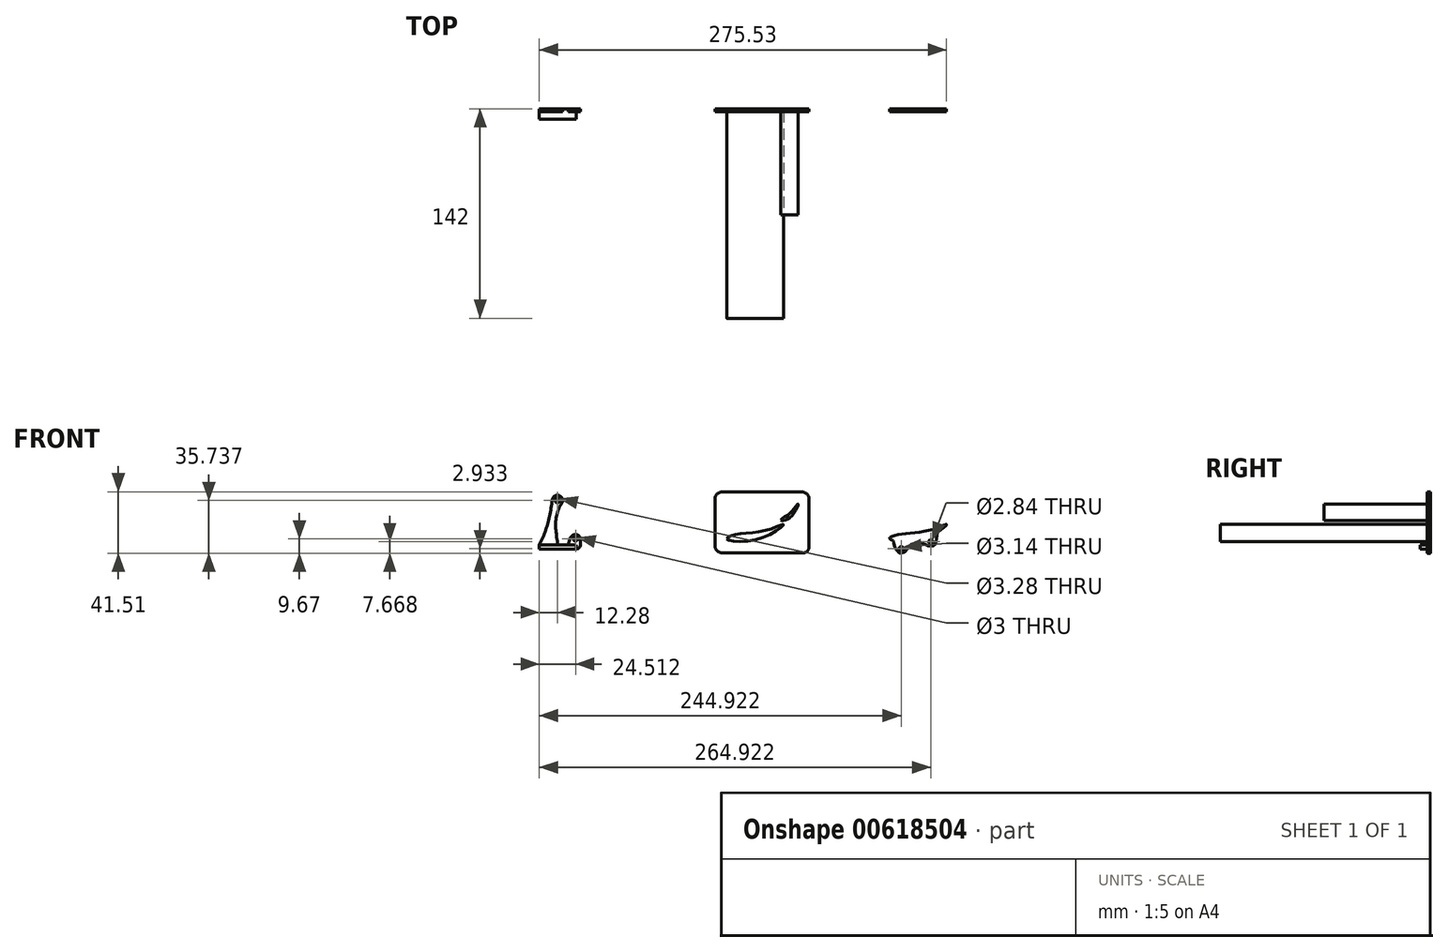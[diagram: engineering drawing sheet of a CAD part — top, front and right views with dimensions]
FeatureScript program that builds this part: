
annotation { "Feature Type Name" : "Feature", "Feature Type Description" : "" }
export const myFeature = defineFeature(function(context is Context, id is Id, definition is map)
    precondition{}
    {
        {
            var Q0;
            Q0=qCreatedBy(makeId("Front.planeOp"),FACE);
            var sketch = newSketch(context, id + "F0", { "sketchPlane" : qUnion([Q0])});
            skFitSpline(sketch, "E0", {"points": [v(-21.95, 0) * mm, v(-17.13, 2.69) * mm, v(5.75, 6.06) * mm, v(16.35, 9.67) * mm, v(0, 0) * mm, v(-21.95, 0) * mm]});
            skLineSegment(sketch, "E1.bottom", {"start": v(-25.09, 31.84) * mm, "end": v(28.72, 31.84) * mm});
            skLineSegment(sketch, "E1.top", {"start": v(-25.09, -9.5) * mm, "end": v(29.72, -9.5) * mm});
            skLineSegment(sketch, "E1.left", {"start": v(-30.09, 26.84) * mm, "end": v(-30.09, -4.5) * mm});
            skLineSegment(sketch, "E1.right", {"start": v(33.72, 26.84) * mm, "end": v(33.72, -5.5) * mm});
            skFitSpline(sketch, "E2", {"points": [v(14.58, 12.66) * mm, v(16.45, 12.46) * mm, v(22.75, 16.4) * mm, v(26.19, 23.58) * mm, v(22.65, 19.35) * mm, v(17.53, 15.02) * mm, v(15.17, 13.64) * mm, v(14.58, 12.66) * mm]});
            skPoint(sketch, "E3.visualSharp", {"position": v(-30.09, 31.84) * mm});
            skArc(sketch, "E3.filletArc", {"start": v(-25.09, 31.84) * mm, "mid": v(-28.62, 30.38) * mm, "end": v(-30.09, 26.84) * mm});
            skPoint(sketch, "E4.visualSharp", {"position": v(33.72, 31.84) * mm});
            skArc(sketch, "E4.filletArc", {"start": v(33.72, 26.84) * mm, "mid": v(32.26, 30.38) * mm, "end": v(28.72, 31.84) * mm});
            skPoint(sketch, "E5.visualSharp", {"position": v(33.72, -9.5) * mm});
            skArc(sketch, "E5.filletArc", {"start": v(29.72, -9.5) * mm, "mid": v(32.55, -8.32) * mm, "end": v(33.72, -5.5) * mm});
            skPoint(sketch, "E6.visualSharp", {"position": v(-30.09, -9.5) * mm});
            skArc(sketch, "E6.filletArc", {"start": v(-30.09, -4.5) * mm, "mid": v(-28.62, -8.03) * mm, "end": v(-25.09, -9.5) * mm});
            skFitSpline(sketch, "E7", {"points": [v(88.34, 0.01) * mm, v(93.16, 2.7) * mm, v(116.04, 6.07) * mm, v(126.64, 9.69) * mm, v(110.29, 0.01) * mm, v(88.34, 0.01) * mm]});
            skCircle(sketch, "E8", {"center": v(96.03, -6.74) * mm, "radius": 1.57 * mm});
            skCircle(sketch, "E9", {"center": v(116.03, -2) * mm, "radius": 1.42 * mm});
            skFitSpline(sketch, "E10", {"points": [v(90.66, -1.14) * mm, v(92.2, -6.56) * mm, v(95.68, -9.63) * mm, v(99, -8.15) * mm, v(101.56, -4.52) * mm, v(105.9, -3.07) * mm, v(110.58, -2.98) * mm, v(114.74, -4.95) * mm, v(118, -4.51) * mm, v(119.74, -1.36) * mm, v(120.48, 4.65) * mm], "startDerivative": vector(14.44, -40.22) * mm, "endDerivative": vector(3.37, 54.45) * mm});
            skLineSegment(sketch, "E11.bottom", {"start": v(-148.9, -3.93) * mm, "end": v(-123.9, -3.93) * mm});
            skLineSegment(sketch, "E11.top", {"start": v(-148.9, -6.93) * mm, "end": v(-123.9, -6.93) * mm});
            skLineSegment(sketch, "E11.left", {"start": v(-148.9, -3.93) * mm, "end": v(-148.9, -6.93) * mm});
            skLineSegment(sketch, "E11.right", {"start": v(-123.9, -3.93) * mm, "end": v(-123.9, -6.93) * mm});
            skCircle(sketch, "E12", {"center": v(-136.61, 26.07) * mm, "radius": 1.64 * mm});
            skCircle(sketch, "E13", {"center": v(-136.61, 26.07) * mm, "radius": 3.5 * mm});
            skCircle(sketch, "E14", {"center": v(-124.38, 0) * mm, "radius": 1.5 * mm});
            skFitSpline(sketch, "E15", {"points": [v(-129.26, -3.93) * mm, v(-127.1, 1.74) * mm, v(-123.94, 2.98) * mm, v(-121.67, 1.33) * mm, v(-120.98, -3.54) * mm, v(-123.9, -6.93) * mm], "startDerivative": vector(6.66, 28.3) * mm, "endDerivative": vector(-29.93, -0.77) * mm});
            skFitSpline(sketch, "E16", {"points": [v(-140.08, 26.51) * mm, v(-148.9, -3.93) * mm], "startDerivative": vector(-4.51, -33.14) * mm, "endDerivative": vector(-15.15, -27.47) * mm});
            skFitSpline(sketch, "E17", {"points": [v(-133.53, 24.4) * mm, v(-136.4, -3.93) * mm], "startDerivative": vector(-19.1, -29.07) * mm, "endDerivative": vector(3.74, -28.88) * mm});
            skSolve(sketch);
        }
        {
            var Q0;
            Q0=makeQuery(id+"F0.imprint","IMPRINT",FACE,{"disambiguationData":[TD([[makeQuery(id+"F0.imprint","IMPRINT",EDGE,{"derivedFrom":sQuery(id+"F0.wireOp",EDGE,"E0")}),-1.0]])]});
            var Q1;
            Q1=makeQuery(id+"F0.imprint","IMPRINT",FACE,{"disambiguationData":[TD([[makeQuery(id+"F0.imprint","IMPRINT",EDGE,{"derivedFrom":sQuery(id+"F0.wireOp",EDGE,"E2")}),1.0]])]});
            extrude(context, id + "F1", {"entities" : qUnion([Q0, Q1]), "depth" : 70 * mm, "offsetDistance" : 25 * mm});
        }
        {
            var Q0;
            Q0 = qSketchRegion(id + "F0", true);
            var Q1;
            Q1=makeQuery(id+"F0.imprint","IMPRINT",FACE,{"disambiguationData":[TD([[makeQuery(id+"F0.imprint","IMPRINT",EDGE,{"derivedFrom":sQuery(id+"F0.wireOp",EDGE,"E0")}),-1.0]])]});
            var Q2;
            Q2=makeQuery(id+"F0.imprint","IMPRINT",FACE,{"disambiguationData":[TD([[makeQuery(id+"F0.imprint","IMPRINT",EDGE,{"derivedFrom":sQuery(id+"F0.wireOp",EDGE,"E2")}),1.0]])]});
            extrude(context, id + "F2", {"entities" : qUnion([Q0, Q1, Q2]), "oppositeDirection" : true, "depth" : 2 * mm, "offsetDistance" : 25 * mm});
        }
        {
            var Q0;
            Q0=makeQuery(id+"F1.opExtrude","SWEPT_BODY",BODY,{"disambiguationData":[OSD([sQuery(id+"F0.wireOp",EDGE,"E0")])]});
            var Q1;
            Q1=makeQuery(id+"F1.opExtrude","CAP_FACE",FACE,{"disambiguationData":[OSD([sQuery(id+"F0.wireOp",EDGE,"E0")])],"isStart":false});
            mirror(context, id + "F3", {"operationType" : NewBodyOperationType.ADD, "entities" : qUnion([Q0]), "mirrorPlane" : qUnion([Q1])});
        }
        {
            var Q0;
            Q0=makeQuery(id+"F0.imprint","IMPRINT",FACE,{"disambiguationData":[TD([[makeQuery(id+"F0.imprint","IMPRINT",EDGE,{"derivedFrom":sQuery(id+"F0.wireOp",EDGE,"E11.top")}),1.0]])]});
            extrude(context, id + "F4", {"entities" : qUnion([Q0]), "operationType" : NewBodyOperationType.ADD, "depth" : 5 * mm, "offsetDistance" : 25 * mm});
        }
    });
